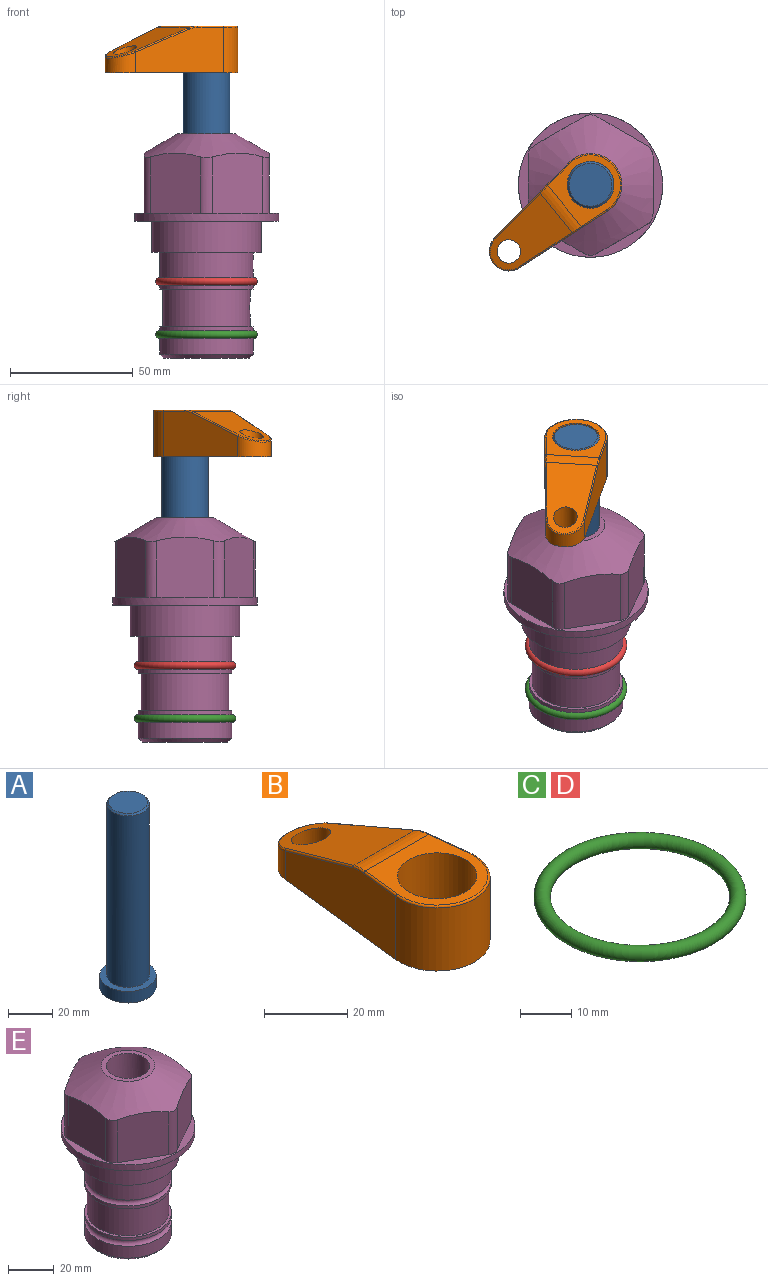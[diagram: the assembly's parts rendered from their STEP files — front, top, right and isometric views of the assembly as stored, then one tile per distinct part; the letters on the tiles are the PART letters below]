
ASSEMBLY  parts=5 mates=3
PART A: 6 faces, bbox 25.4x25.4x101.6 mm
  f0: plane 17.46x17.46mm, normal (0,0,1), area 239.5mm2, adj f5
  f1: plane 25.4x25.4mm, normal (0,0,-1), area 506.7mm2, adj f2
  f2: cylinder r=12.7mm len=25.4mm, axis (0,0,1), area 506.7mm2, adj f1,f3
  f3: plane 25.4x25.4mm, normal (0,0,1), area 221.7mm2, adj f2,f4
  f4: cylinder r=9.53mm len=94.46mm, axis (0,0,1), area 5653mm2, adj f3,f5
  f5: cone r=8.73mm half-angle=45deg, axis (0,0,-1), area 64.4mm2, adj f0,f4
PART B: 44 faces, bbox 27.5x64.5x19.1 mm
  f0: plane 2.3x0.95mm, normal (0,0,-1), area 1mm2, adj f25,f30,f34
  f1: plane 63.5x25.4mm, normal (0,0,-1), area 561.7mm2, adj f2,f3,f4,f5,f6,f7,f19,f20
  f2: cylinder r=12.7mm len=25.4mm, axis (0,0,-1), area 792.2mm2, adj f1,f3,f5,f13
  f3: plane 42.33x18.54mm, normal (0.99,0.11,0), area 647mm2, adj f1,f2,f4,f11,f12,f14
  f4: cylinder r=7.94mm len=15.78mm, axis (0,0,-1), area 158.6mm2, adj f1,f3,f5,f16
  f5: plane 42.33x18.54mm, normal (-0.99,0.11,0), area 647mm2, adj f1,f2,f4,f15,f17,f18
  f6: cylinder r=9.53mm len=19.05mm, axis (0,0,-1), area 1140.1mm2, adj f1,f8
  f7: cylinder r=4.76mm len=10.98mm, axis (0,0,-1), area 276.1mm2, adj f1,f9
  f8: plane 25.83x24.38mm, normal (0,0,1), area 262.2mm2, adj f6,f10,f11,f13,f15
  f9: plane 32.49x20.55mm, normal (0,0.34,0.94), area 489.9mm2, adj f7,f10,f14,f16,f18
  f10: cylinder r=12.7mm len=21.49mm, axis (-1,0,0), area 93.2mm2, adj f8,f9,f12,f17
  f11: cylinder r=0.51mm len=12.34mm, axis (0.11,-0.99,0), area 9.9mm2, adj f3,f8,f12,f13
  f12: bspline ~7.62x1.64mm, area 3.5mm2, adj f3,f10,f11,f14
  f13: torus R=12.19mm, axis (0,0,1), area 33.6mm2, adj f2,f8,f11,f15
  f14: cylinder r=0.51mm len=26.01mm, axis (0.1,-0.93,0.34), area 21.6mm2, adj f3,f9,f12,f16
  f15: cylinder r=0.51mm len=12.34mm, axis (0.11,0.99,0), area 9.9mm2, adj f5,f8,f13,f17
  f16: bspline ~15.78x7.05mm, area 15.7mm2, adj f4,f9,f14,f18
  f17: bspline ~7.62x1.64mm, area 3.5mm2, adj f5,f10,f15,f18
  f18: cylinder r=0.51mm len=26.01mm, axis (0.1,0.93,-0.34), area 21.6mm2, adj f5,f9,f16,f17
  f19: plane 21.6x14.29mm, normal (-0.99,-0.11,0), area 242.6mm2, adj f1,f26,f28,f34,f36,f38
  f20: plane 21.6x14.29mm, normal (0.99,-0.11,0), area 242.6mm2, adj f1,f27,f29,f37,f39,f41
  f21: cylinder r=12.7mm len=14.29mm, axis (0,0,-1), area 173.2mm2, adj f1,f26,f27,f30,f31,f33
  f22: cylinder r=7.94mm len=7.63mm, axis (0,0,-1), area 53.8mm2, adj f1,f28,f29,f42
  f23: plane 2.3x0.95mm, normal (0,0,-1), area 1mm2, adj f25,f33,f37
  f24: plane 17.94x12.32mm, normal (0,-0.34,-0.94), area 191.2mm2, adj f25,f38,f41,f42
  f25: cylinder r=9.53mm len=12.93mm, axis (-1,0,0), area 37.5mm2, adj f0,f23,f24,f31,f36,f39
  f26: cylinder r=1.59mm len=14.29mm, axis (0,0,-1), area 49mm2, adj f1,f19,f21,f32
  f27: cylinder r=1.59mm len=14.29mm, axis (0,0,-1), area 49mm2, adj f1,f20,f21,f35
  f28: cylinder r=1.59mm len=7.28mm, axis (0,0,-1), area 22.1mm2, adj f1,f19,f22,f40
  f29: cylinder r=1.59mm len=7.28mm, axis (0,0,-1), area 22.1mm2, adj f1,f20,f22,f43
  f30: torus R=14.29mm, axis (0,0,1), area 5.8mm2, adj f0,f21,f31,f32
  f31: bspline ~11.06x2.73mm, area 20.8mm2, adj f21,f25,f30,f33
  f32: sphere r=1.59mm, area 5.4mm2, adj f26,f30,f34
  f33: torus R=14.29mm, axis (0,0,1), area 5.8mm2, adj f21,f23,f31,f35
  f34: cylinder r=1.59mm len=1.68mm, axis (-0.11,0.99,0), area 2.4mm2, adj f0,f19,f32,f36
  f35: sphere r=1.59mm, area 5.4mm2, adj f27,f33,f37
  f36: bspline ~5.82x2.33mm, area 7.7mm2, adj f19,f25,f34,f38
  f37: cylinder r=1.59mm len=1.68mm, axis (0.11,0.99,0), area 2.4mm2, adj f20,f23,f35,f39
  f38: cylinder r=1.59mm len=18.33mm, axis (0.1,-0.93,0.34), area 46.7mm2, adj f19,f24,f36,f40
  f39: bspline ~5.82x2.33mm, area 7.7mm2, adj f20,f25,f37,f41
  f40: sphere r=1.59mm, area 3.6mm2, adj f28,f38,f42
  f41: cylinder r=1.59mm len=18.33mm, axis (0.1,0.93,-0.34), area 46.7mm2, adj f20,f24,f39,f43
  f42: bspline ~8.31x1.84mm, area 15.3mm2, adj f22,f24,f40,f43
  f43: sphere r=1.59mm, area 3.6mm2, adj f29,f41,f42
PART C: 1 faces, bbox 44.7x44.7x3.2 mm
  f0: torus R=19.05mm, axis (0,0,1), area 1193.9mm2
PART D: same geometry as C
PART E: 36 faces, bbox 58.7x58.7x91.2 mm
  f0: cylinder r=17.78mm len=35.56mm, axis (0,0,1), area 1670.8mm2, adj f23,f24,f31
  f1: cylinder r=19.05mm len=38.1mm, axis (0,0,1), area 1191.9mm2, adj f26,f27,f30
  f2: plane 58.66x58.66mm, normal (0,0,-1), area 1150.6mm2, adj f3,f28
  f3: cylinder r=29.33mm len=58.66mm, axis (0,0,-1), area 585.1mm2, adj f2,f4
  f4: plane 58.66x58.66mm, normal (0,0,1), area 475.9mm2, adj f3,f5,f6,f7,f8,f9,f10,f11
  f5: plane 24.5x20.32mm, normal (-0.5,0.87,0), area 562.8mm2, adj f4,f15,f16,f17
  f6: plane 24.5x20.32mm, normal (0.5,0.87,0), area 562.8mm2, adj f4,f14,f15,f17
  f7: plane 24.5x23.48mm, normal (1,0,0), area 562.8mm2, adj f4,f13,f14,f17
  f8: plane 24.5x20.32mm, normal (0.5,-0.87,0), area 562.8mm2, adj f4,f12,f13,f17
  f9: plane 24.5x20.32mm, normal (-0.5,-0.87,0), area 562.8mm2, adj f4,f11,f12,f17
  f10: plane 24.5x23.48mm, normal (-1,0,0), area 562.8mm2, adj f4,f11,f16,f17
  f11: cylinder r=5.08mm len=23.01mm, axis (0,0,-1), area 121.2mm2, adj f4,f9,f10,f17
  f12: cylinder r=5.08mm len=23.01mm, axis (0,0,-1), area 121.2mm2, adj f4,f8,f9,f17
  f13: cylinder r=5.08mm len=23.01mm, axis (0,0,-1), area 121.2mm2, adj f4,f7,f8,f17
  f14: cylinder r=5.08mm len=23.01mm, axis (0,0,-1), area 121.2mm2, adj f4,f6,f7,f17
  f15: cylinder r=5.08mm len=23.01mm, axis (0,0,-1), area 121.2mm2, adj f4,f5,f6,f17
  f16: cylinder r=5.08mm len=23.01mm, axis (0,0,-1), area 121.2mm2, adj f4,f5,f10,f17
  f17: cone r=11.73mm half-angle=60deg, axis (0,0,-1), area 2071.8mm2, adj f5,f6,f7,f8,f9,f10,f11,f12
  f18: plane 23.46x23.46mm, normal (0,0,1), area 147.4mm2, adj f17,f35
  f19: plane 34.93x34.93mm, normal (0,0,-1), area 958mm2, adj f29
  f20: cylinder r=19.05mm len=38.1mm, axis (0,0,1), area 760.1mm2, adj f21,f29
  f21: torus R=19.05mm, axis (0,0,1), area 565.3mm2, adj f20,f22
  f22: cylinder r=19.05mm len=38.1mm, axis (0,0,1), area 190mm2, adj f21,f23
  f23: plane 38.1x38.1mm, normal (0,0,1), area 146.9mm2, adj f0,f22
  f24: plane 38.1x38.1mm, normal (0,0,-1), area 146.9mm2, adj f0,f25
  f25: cylinder r=19.05mm len=38.1mm, axis (0,0,1), area 190mm2, adj f24,f26
  f26: torus R=19.05mm, axis (0,0,1), area 565.3mm2, adj f1,f25
  f27: plane 44.45x44.45mm, normal (0,0,-1), area 411.7mm2, adj f1,f28
  f28: cylinder r=22.23mm len=44.45mm, axis (0,0,1), area 1773.5mm2, adj f2,f27
  f29: cone r=19.05mm half-angle=45deg, axis (0,0,1), area 257.5mm2, adj f19,f20
  f30: cylinder r=3.17mm len=6.75mm, axis (-1,0,0), area 128mm2, adj f1,f33
  f31: cylinder r=3.17mm len=6.35mm, axis (-1,0,0), area 102.5mm2, adj f0,f33
  f32: plane 25.4x25.4mm, normal (0,0,1), area 506.7mm2, adj f33
  f33: cylinder r=12.7mm len=66.42mm, axis (0,0,-1), area 5236.2mm2, adj f30,f31,f32,f34
  f34: cone r=9.53mm half-angle=30deg, axis (0,0,-1), area 443.4mm2, adj f33,f35
  f35: cylinder r=9.53mm len=19.05mm, axis (0,0,-1), area 849mm2, adj f18,f34
PLACE A rot(axis=(0,0,-1),140.8deg) t=(0,0,5.71)mm
PLACE B rot(axis=(0,0,1),129.2deg) t=(0,0,60.32)mm
PLACE C t=(0,0,-21.59)mm
PLACE D at identity
PLACE E at identity fixed
MATE fastened C.f0 <-> E.f0  axis (0,0,1) through (0,0,-46.1)mm
MATE cylindrical A.f2 <-> E.f0  axis (0,0,1) through (0,0,31.34)mm
MATE fastened B.f2 <-> A.f2  axis (0,0,1) through (0,0,79.37)mm
